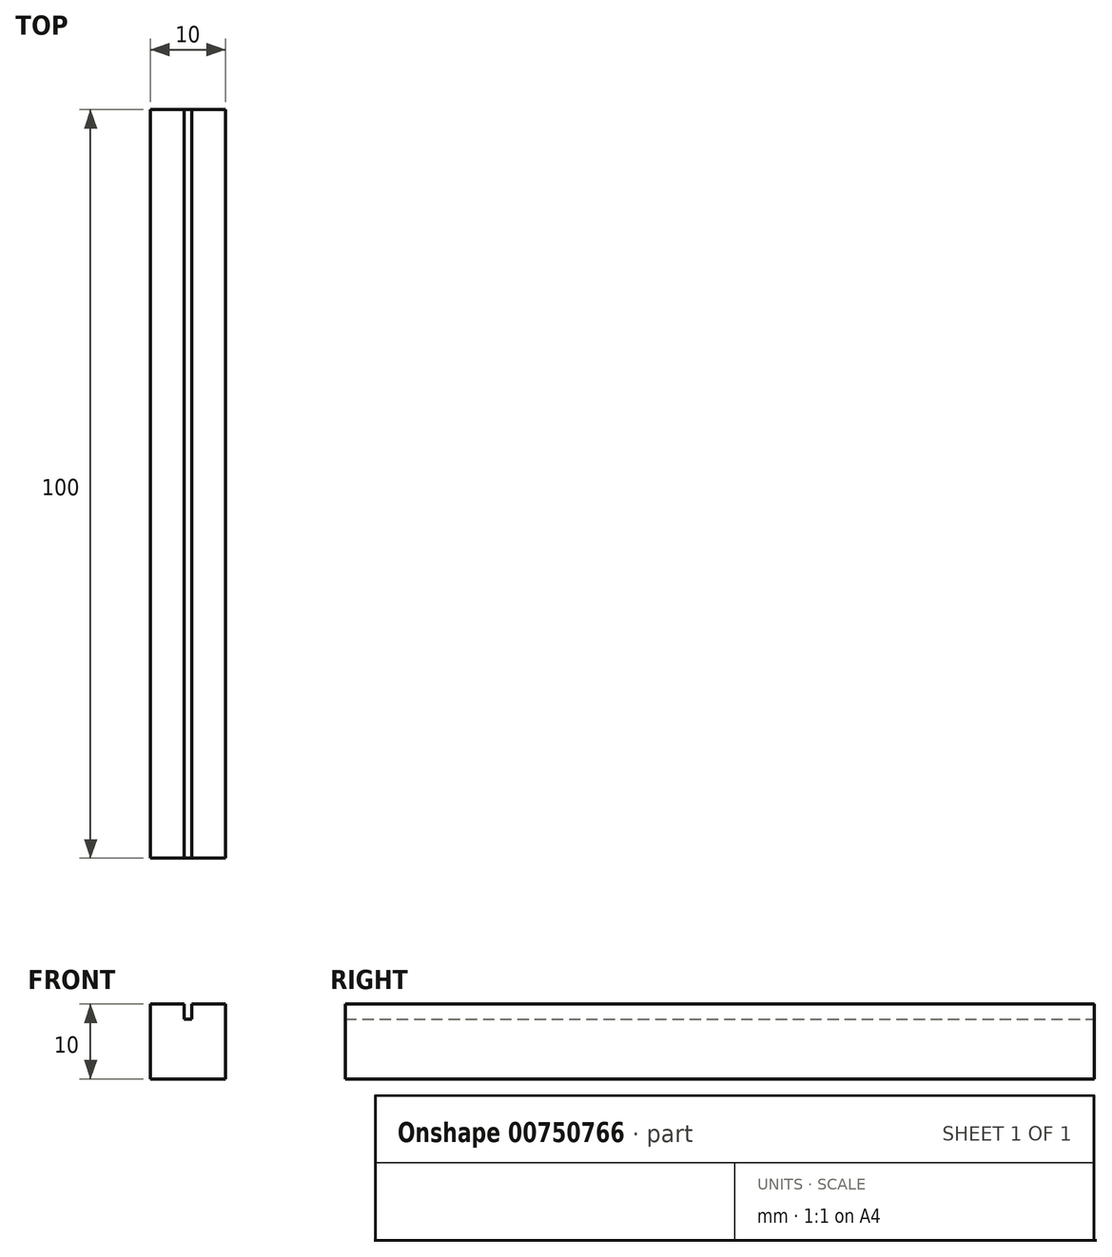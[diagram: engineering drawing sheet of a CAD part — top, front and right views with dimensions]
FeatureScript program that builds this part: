
annotation { "Feature Type Name" : "Feature", "Feature Type Description" : "" }
export const myFeature = defineFeature(function(context is Context, id is Id, definition is map)
    precondition{}
    {
        {
            var Q0;
            Q0=qCreatedBy(makeId("Front.planeOp"),FACE);
            var sketch = newSketch(context, id + "F0", { "sketchPlane" : qUnion([Q0])});
            skLineSegment(sketch, "E0.bottom", {"start": v(0, 0) * mm, "end": v(10, 0) * mm});
            skLineSegment(sketch, "E0.top", {"start": v(0, 10) * mm, "end": v(4.5, 10) * mm});
            skLineSegment(sketch, "E0.left", {"start": v(0, 0) * mm, "end": v(0, 10) * mm});
            skLineSegment(sketch, "E0.right", {"start": v(10, 0) * mm, "end": v(10, 10) * mm});
            skLineSegment(sketch, "E1.top", {"start": v(4.5, 8) * mm, "end": v(5.5, 8) * mm});
            skLineSegment(sketch, "E1.left", {"start": v(4.5, 10) * mm, "end": v(4.5, 8) * mm});
            skLineSegment(sketch, "E1.right", {"start": v(5.5, 10) * mm, "end": v(5.5, 8) * mm});
            skLineSegment(sketch, "E2.trimOffspring", {"start": v(5.5, 10) * mm, "end": v(10, 10) * mm});
            skSolve(sketch);
        }
        {
            var Q0;
            Q0=makeQuery(id+"F0.imprint","IMPRINT",FACE,{"disambiguationData":[TD([[makeQuery(id+"F0.imprint","IMPRINT",EDGE,{"derivedFrom":sQuery(id+"F0.wireOp",EDGE,"E0.bottom")}),1.0]])]});
            extrude(context, id + "F1", {"entities" : qUnion([Q0]), "depth" : 100 * mm, "offsetDistance" : 25 * mm});
        }
    });
